# Revit family: BIG-500-O
name_source: partatom
category: Plumbing Fixtures
units: mm (PartAtom-declared; Revit-internal decimal feet)

## family parameters
Always vertical = Yes
Cut with Voids When Loaded = Yes
OmniClass Number = 23.45.00.00
OmniClass Title = Sanitary, Laundry, and Cleaning Equipment
Part Type = Normal
Room Calculation Point = No
Round Connector Dimension = Use Diameter
Shared = No
Work Plane-Based = No

## types (1)
- BIG-500-O
    Bottom Pipe RP = 3/4"
    Default Elevation = 0"
    Ext End = -23 5/16"
    Front Extude = 13 1/2"
    Height of Body = 26"
    Length = 37"
    Lid Height from Inlet/Outlet Center (15.5" Min. thru 24.5" Max.) = 24 1/2"
    Manufacturer = MIFAB
    Material = Polyethylene, High Density
    Model = BIG-500-O
    Pipe RP = 13 1/2"
    Top RP 1 = 9"
    Top Vent = 9 7/16"
    URL = WWW.MIFAB.COM
    Vent = 20"
    Vent Pipe = 0"
    Vent height = 16 1/4"
    Vent/2 = 10"
    Vesibility-Vent = Yes
    Visibility-1 = Yes
    Visiblity = No
    Void 1 H = 3"
    Void 1 L = 3"
    Void 1 TL = 6"
    Width = 28"
    array = 2
    center void = 2"
    center void h = 2"
    pipe height = 12 3/4"
    v1 = No
    v2 = No

## geometry (parser evidence)
native form markers: Sweep x11
no freeform markers — native parametric forms only
